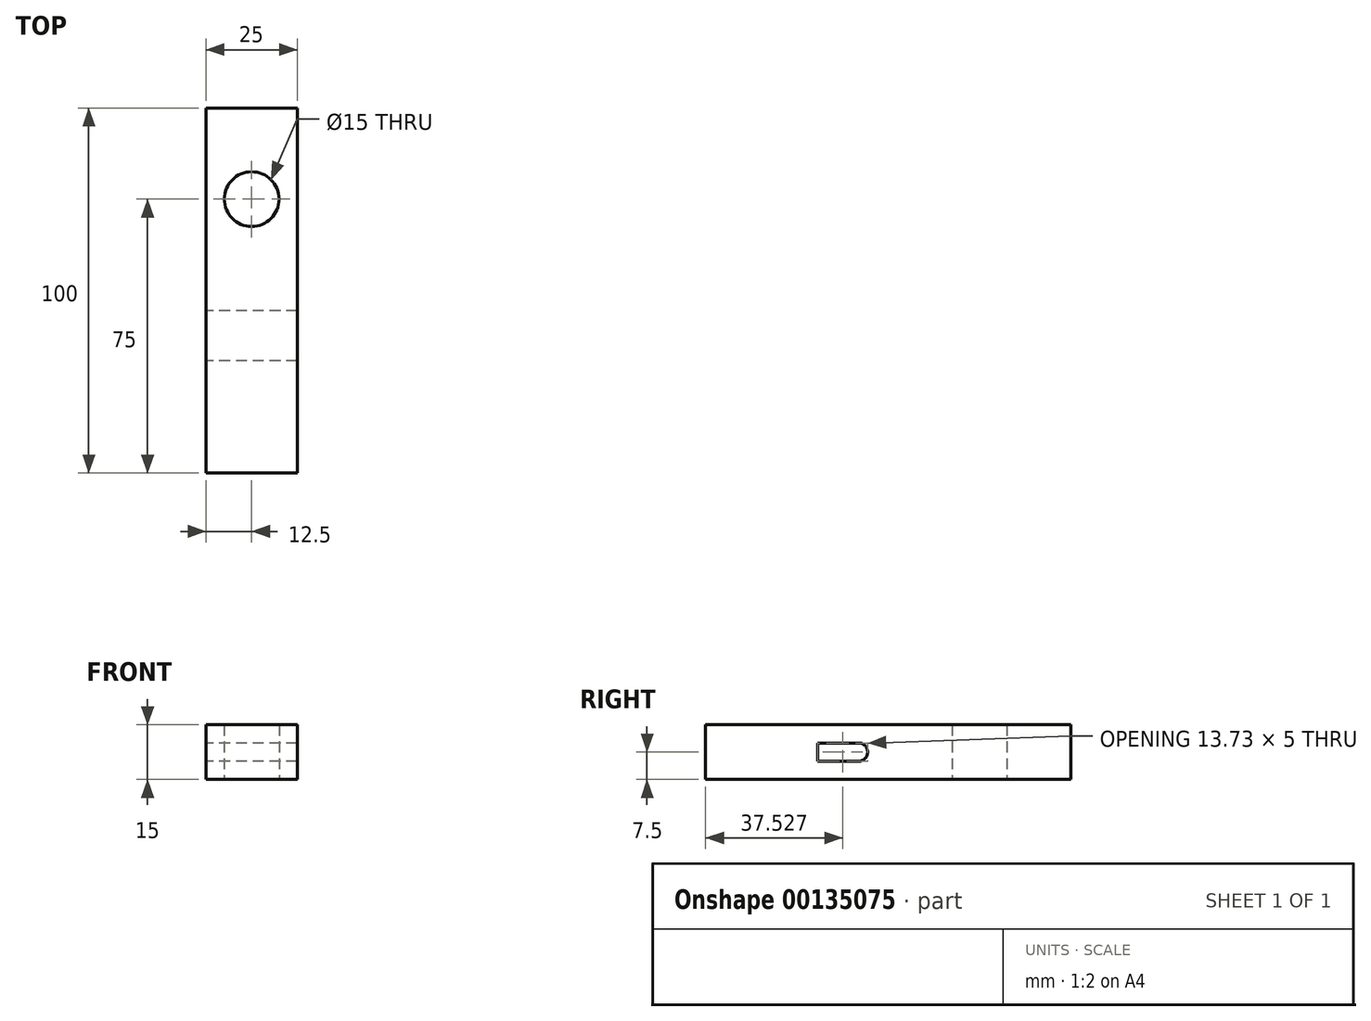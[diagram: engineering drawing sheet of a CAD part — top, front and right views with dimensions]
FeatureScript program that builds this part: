
annotation { "Feature Type Name" : "Feature", "Feature Type Description" : "" }
export const myFeature = defineFeature(function(context is Context, id is Id, definition is map)
    precondition{}
    {
        {
            var Q0;
            Q0=qCreatedBy(makeId("Top.planeOp"),FACE);
            var sketch = newSketch(context, id + "F2", { "sketchPlane" : qUnion([Q0])});
            skLineSegment(sketch, "E0.bottom", {"start": v(-12.5, 50) * mm, "end": v(12.5, 50) * mm});
            skLineSegment(sketch, "E0.top", {"start": v(-12.5, -50) * mm, "end": v(12.5, -50) * mm});
            skLineSegment(sketch, "E0.left", {"start": v(-12.5, 50) * mm, "end": v(-12.5, -50) * mm});
            skLineSegment(sketch, "E0.right", {"start": v(12.5, 50) * mm, "end": v(12.5, -50) * mm});
            skPoint(sketch, "E0.middle", {"position": v(0, 0) * mm});
            skLineSegment(sketch, "E1", {"start": v(0, 50) * mm, "end": v(0, -50) * mm, "construction": true});
            skCircle(sketch, "E2", {"center": v(0, 25) * mm, "radius": 7.5 * mm});
            skSolve(sketch);
        }
        {
            var Q0;
            Q0 = qSketchRegion(id + "F2", true);
            extrude(context, id + "F0", {"entities" : qUnion([Q0]), "depth" : 15 * mm});
        }
        {
            var Q0;
            Q0=makeQuery(id+"F0.opExtrude","SWEPT_FACE",FACE,{"disambiguationData":[OSD([sQuery(id+"F2.wireOp",EDGE,"E0.left")])]});
            var sketch = newSketch(context, id + "F3", { "sketchPlane" : qUnion([Q0])});
            skLineSegment(sketch, "E3.bottom", {"start": v(19.34, 5) * mm, "end": v(8.1, 5) * mm});
            skLineSegment(sketch, "E3.top", {"start": v(19.34, 10) * mm, "end": v(8.1, 10) * mm});
            skLineSegment(sketch, "E3.left", {"start": v(19.34, 5) * mm, "end": v(19.34, 10) * mm});
            skLineSegment(sketch, "E3.right", {"start": v(8.1, 5) * mm, "end": v(8.1, 10) * mm, "construction": true});
            skArc(sketch, "E4", {"start": v(8.1, 10) * mm, "mid": v(5.6, 7.5) * mm, "end": v(8.1, 5) * mm});
            skLineSegment(sketch, "E5.0", {"start": v(-50, 0) * mm, "end": v(50, 0) * mm});
            skSolve(sketch);
        }
        {
            var Q0;
            Q0 = qSketchRegion(id + "F3", true);
            extrude(context, id + "F1", {"entities" : qUnion([Q0]), "operationType" : NewBodyOperationType.REMOVE, "endBound" : BoundingType.UP_TO_NEXT, "oppositeDirection" : true, "depth" : 25 * mm});
        }
    });
